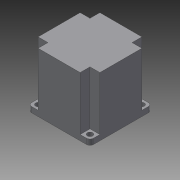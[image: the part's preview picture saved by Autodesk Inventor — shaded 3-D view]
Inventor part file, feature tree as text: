
AUTODESK INVENTOR PART (.ipt)
format: ipt  version: 2015 (Build 190159000, 159)  size: 142,336 bytes
history: native  units: in
note: dims shown in document units (in); Inventor stores cm internally (conversion verified against a paired STEP export)
features: extrude x4, sketch x3, fillet x2
ambient origin geometry x8: Origin, YZ Plane, XZ Plane, XY Plane, X Axis, Y Axis, Z Axis, Center Point
bodies: Solid1 (feature_tree)
feature tree (9):
  sketch  "Sketch1"  dims[d0=2.2205in d1=2.2205in]
  extrude  "Extrusion1"  Depth=2.2205in
  extrude  "Extrusion2"  Depth=0.3543in
  fillet  "Fillet1"  Radius=2.126in
  extrude  "Extrusion3"  Depth=0.01in
  extrude  "Extrusion4"  Depth=0.1969in
  fillet  "Fillet2"  Radius=0.1969in
  sketch  "Sketch2"  dims[d2=0.3543in d3=0.3543in d4=2.126in d5=0.0in]
  sketch  "Sketch3"  dims[d6=1.8559in d7=1.8559in d8=0.1969in d9=0.1969in d10=0.0in d11=0.125in d12=1.5in d13=0.063in d14=0.0in d15=0.25in d16=0.8268in d17=0.0in d18=0.01in]
